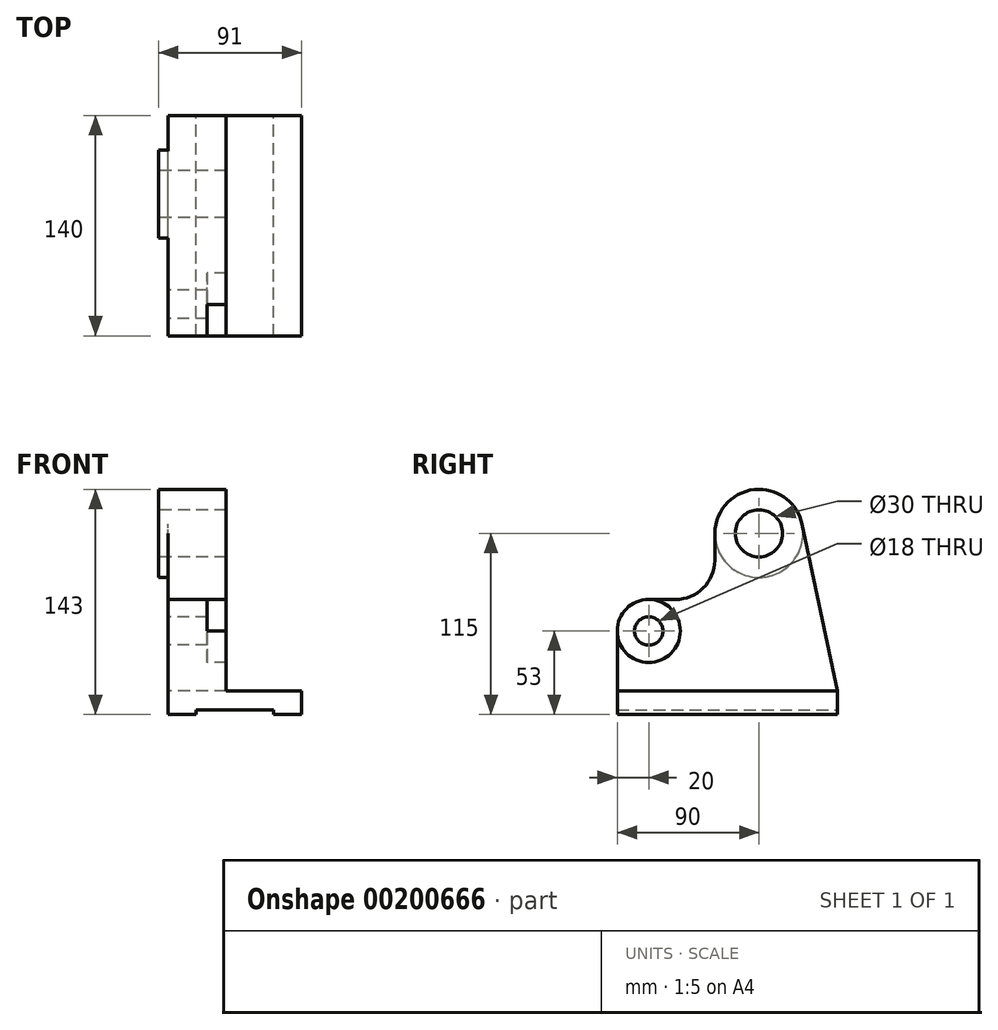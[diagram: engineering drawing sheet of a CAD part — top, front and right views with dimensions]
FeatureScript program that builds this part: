
annotation { "Feature Type Name" : "Feature", "Feature Type Description" : "" }
export const myFeature = defineFeature(function(context is Context, id is Id, definition is map)
    precondition{}
    {
        {
            var Q0;
            Q0=qCreatedBy(makeId("Front.planeOp"),FACE);
            var sketch = newSketch(context, id + "F0", { "sketchPlane" : qUnion([Q0])});
            skLineSegment(sketch, "E0", {"start": v(-42.5, 0) * mm, "end": v(-24.5, 0) * mm});
            skLineSegment(sketch, "E1", {"start": v(-24.5, 0) * mm, "end": v(-24.5, 3) * mm});
            skLineSegment(sketch, "E2", {"start": v(-24.5, 3) * mm, "end": v(24.5, 3) * mm});
            skLineSegment(sketch, "E3", {"start": v(24.5, 3) * mm, "end": v(24.5, 0) * mm});
            skLineSegment(sketch, "E4", {"start": v(24.5, 0) * mm, "end": v(42.5, 0) * mm});
            skLineSegment(sketch, "E5", {"start": v(42.5, 0) * mm, "end": v(42.5, 15) * mm});
            skLineSegment(sketch, "E6", {"start": v(42.5, 15) * mm, "end": v(-42.5, 15) * mm});
            skLineSegment(sketch, "E7", {"start": v(-42.5, 15) * mm, "end": v(-42.5, 0) * mm});
            skSolve(sketch);
        }
        {
            var Q0;
            Q0 = qSketchRegion(id + "F0", true);
            var Q1;
            Q1=makeQuery(id+"F0.imprint","IMPRINT",FACE,{"disambiguationData":[TD([[makeQuery(id+"F0.imprint","IMPRINT",EDGE,{"derivedFrom":sQuery(id+"F0.wireOp",EDGE,"E0")}),1.0]])]});
            extrude(context, id + "F1", {"entities" : qUnion([Q0, Q1]), "depth" : 140 * mm});
        }
        {
            var Q0;
            Q0=makeQuery(id+"F1.opExtrude","SWEPT_FACE",FACE,{"disambiguationData":[OSD([sQuery(id+"F0.wireOp",EDGE,"E7")])]});
            var sketch = newSketch(context, id + "F2", { "sketchPlane" : qUnion([Q0])});
            skCircle(sketch, "E8", {"center": v(50, 115) * mm, "radius": 28 * mm});
            skCircle(sketch, "E9", {"center": v(50, 115) * mm, "radius": 15 * mm});
            skPoint(sketch, "E10.orphan", {"position": v(50, 15) * mm});
            skLineSegment(sketch, "E11", {"start": v(50, 115) * mm, "end": v(50, 15) * mm, "construction": true});
            skLineSegment(sketch, "E12", {"start": v(50, 115) * mm, "end": v(50, 144.68) * mm, "construction": true});
            skLineSegment(sketch, "E13", {"start": v(0, 15) * mm, "end": v(22.62, 120.85) * mm});
            skCircle(sketch, "E14", {"center": v(120, 53) * mm, "radius": 20 * mm});
            skCircle(sketch, "E15", {"center": v(120, 53) * mm, "radius": 9 * mm});
            skLineSegment(sketch, "E16.0", {"start": v(140, 15) * mm, "end": v(140, 0) * mm});
            skLineSegment(sketch, "E17", {"start": v(140, 15) * mm, "end": v(140, 53) * mm});
            skLineSegment(sketch, "E18", {"start": v(120, 73) * mm, "end": v(103.05, 73) * mm});
            skLineSegment(sketch, "E19", {"start": v(78, 115.09) * mm, "end": v(78.05, 97.92) * mm});
            skPoint(sketch, "E20.visualSharp", {"position": v(78.13, 73) * mm});
            skArc(sketch, "E20.filletArc", {"start": v(78.05, 97.92) * mm, "mid": v(85.4, 80.3) * mm, "end": v(103.05, 73) * mm});
            skSolve(sketch);
        }
        {
            var Q0;
            Q0 = qSketchRegion(id + "F2", true);
            var Q1;
            {var subQ3=sQuery(id+"F2.wireOp",EDGE,"E13");Q1=makeQuery(id+"F2.imprint","IMPRINT",FACE,{"disambiguationData":[TD([[makeQuery(id+"F2.imprint","IMPRINT",EDGE,{"derivedFrom":subQ3}),-1.0]])]});}
            extrude(context, id + "F3", {"entities" : qUnion([Q0, Q1]), "oppositeDirection" : true, "depth" : 25 * mm});
        }
        {
            var Q0;
            Q0=makeQuery(id+"F3.opExtrude","CAP_FACE",FACE,{"disambiguationData":[OSD([sQuery(id+"F0.wireOp",EDGE,"E6"),sQuery(id+"F0.wireOp",EDGE,"E7"),sQuery(id+"F2.wireOp",EDGE,"E8"),sQuery(id+"F2.wireOp",EDGE,"E9"),sQuery(id+"F2.wireOp",EDGE,"E13"),sQuery(id+"F2.wireOp",EDGE,"E14"),sQuery(id+"F2.wireOp",EDGE,"E15"),sQuery(id+"F2.wireOp",EDGE,"E17"),sQuery(id+"F2.wireOp",EDGE,"E18"),sQuery(id+"F2.wireOp",EDGE,"E19"),sQuery(id+"F2.wireOp",EDGE,"E20.filletArc")])],"isStart":false});
            var sketch = newSketch(context, id + "F4", { "sketchPlane" : qUnion([Q0])});
            skCircle(sketch, "E21", {"center": v(-120, 53) * mm, "radius": 20 * mm});
            skSolve(sketch);
        }
        {
            var Q0;
            {var subQ0=sQuery(id+"F4.wireOp",EDGE,"E21");Q0=makeQuery(id+"F4.imprint","IMPRINT",FACE,{"disambiguationData":[TD([[makeQuery(id+"F4.imprint","IMPRINT",EDGE,{"disambiguationData":[OD(0.0)],"derivedFrom":subQ0}),-1.0]])]});}
            extrude(context, id + "F5", {"entities" : qUnion([Q0]), "operationType" : NewBodyOperationType.ADD, "depth" : 12 * mm});
        }
        {
            var Q0;
            Q0=makeQuery(id+"F3.opExtrude","CAP_FACE",FACE,{"disambiguationData":[OSD([sQuery(id+"F0.wireOp",EDGE,"E6"),sQuery(id+"F0.wireOp",EDGE,"E7"),sQuery(id+"F2.wireOp",EDGE,"E8"),sQuery(id+"F2.wireOp",EDGE,"E9"),sQuery(id+"F2.wireOp",EDGE,"E13"),sQuery(id+"F2.wireOp",EDGE,"E14"),sQuery(id+"F2.wireOp",EDGE,"E15"),sQuery(id+"F2.wireOp",EDGE,"E17"),sQuery(id+"F2.wireOp",EDGE,"E18"),sQuery(id+"F2.wireOp",EDGE,"E19"),sQuery(id+"F2.wireOp",EDGE,"E20.filletArc")])],"isStart":true});
            cPlane(context, id + "F6", {"entities" : qUnion([Q0]), "cplaneType" : CPlaneType.OFFSET, "offset" : 12 * mm, "oppositeDirection" : true, "width" : 150 * mm, "height" : 150 * mm});
        }
        {
            var Q0;
            Q0=qCreatedBy(id+"F6.planeOp",FACE);
            var sketch = newSketch(context, id + "F7", { "sketchPlane" : qUnion([Q0])});
            skCircle(sketch, "E22.0", {"center": v(50, 115) * mm, "radius": 15 * mm});
            skCircle(sketch, "E23", {"center": v(50, 115) * mm, "radius": 28 * mm});
            skSolve(sketch);
        }
        {
            var Q0;
            Q0 = qSketchRegion(id + "F7", true);
            extrude(context, id + "F8", {"entities" : qUnion([Q0]), "operationType" : NewBodyOperationType.ADD, "endBound" : BoundingType.SYMMETRIC, "depth" : 36 * mm});
        }
    });
